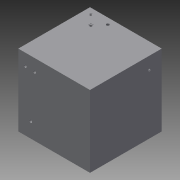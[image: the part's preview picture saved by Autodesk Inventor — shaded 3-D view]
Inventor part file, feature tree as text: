
AUTODESK INVENTOR PART (.ipt)
format: ipt  version: 2014 (Build 180170000, 170)  size: 350,208 bytes
history: native  units: mm
features: other x54, sketch x15, extrude x1
ambient origin geometry x8: Origin, YZ Plane, XZ Plane, XY Plane, X Axis, Y Axis, Z Axis, Center Point
bodies: 实体1 (feature_tree)
feature tree (70):
  extrude  "拉伸1"  TaperAngle=0.0deg  [1 undecoded]
  other  "UCS1"
  other  "UCS2"
  other  "UCS3"
  other  "UCS4"
  other  "UCS5"
  other  "UCS6"
  other  "iFeature7:2"
  other  "iFeature7:3"
  other  "iFeature7:4"
  other  "iFeature7:5"
  other  "iFeature7:6"
  other  "iFeature7:7"
  sketch  "草图1"  dims[d0=400.0mm d1=0.0mm]
  other  "UCS1: YZ 平面"
  other  "UCS1: XZ 平面"
  other  "UCS1: XY 平面"
  other  "UCS1: X 轴"
  other  "UCS1: Y 轴"
  other  "UCS1: Z 轴"
  other  "UCS1: 原点"
  other  "UCS2: YZ 平面"
  other  "UCS2: XZ 平面"
  other  "UCS2: XY 平面"
  other  "UCS2: X 轴"
  other  "UCS2: Y 轴"
  other  "UCS2: Z 轴"
  other  "UCS2: 原点"
  other  "UCS3: YZ 平面"
  other  "UCS3: XZ 平面"
  other  "UCS3: XY 平面"
  other  "UCS3: X 轴"
  other  "UCS3: Y 轴"
  other  "UCS3: Z 轴"
  other  "UCS3: 原点"
  other  "UCS4: YZ 平面"
  other  "UCS4: XZ 平面"
  other  "UCS4: XY 平面"
  other  "UCS4: X 轴"
  other  "UCS4: Y 轴"
  other  "UCS4: Z 轴"
  other  "UCS4: 原点"
  other  "UCS5: YZ 平面"
  other  "UCS5: XZ 平面"
  other  "UCS5: XY 平面"
  other  "UCS5: X 轴"
  other  "UCS5: Y 轴"
  other  "UCS5: Z 轴"
  other  "UCS5: 原点"
  other  "UCS6: YZ 平面"
  other  "UCS6: XZ 平面"
  other  "UCS6: XY 平面"
  other  "UCS6: X 轴"
  other  "UCS6: Y 轴"
  other  "UCS6: Z 轴"
  other  "UCS6: 原点"
  sketch  "草图2"  dims[d2=0.0mm d3=0.0mm d4=0.0mm d5=0.0mm d6=0.0mm d7=0.0mm]
  sketch  "草图3"  dims[d8=0.0mm d9=0.0mm d10=0.0mm d11=0.0mm d12=0.0mm d13=0.0mm]
  sketch  "草图4"  dims[d14=0.0mm d15=0.0mm d16=0.0mm d17=0.0mm d18=0.0mm d19=0.0mm]
  sketch  "草图5"  dims[d20=0.0mm d21=0.0mm d22=0.0mm d23=0.0mm d24=0.0mm d25=0.0mm]
  sketch  "草图6"  dims[d26=0.0mm d27=0.0mm d28=0.0mm d29=0.0mm d30=0.0mm d31=0.0mm]
  sketch  "草图8"  dims[d32=0.0mm d33=0.0mm d34=0.0mm d35=0.0mm d36=0.0mm d37=0.0mm d38=0.0mm]
  sketch  "草图10"  dims[d42=0.0mm]
  sketch  "草图11"  dims[d46=0.0mm]
  sketch  "草图12"  dims[d50=0.0mm]
  sketch  "草图13"  dims[d54=0.0mm]
  sketch  "草图14"  dims[d58=0.0mm]
  sketch  "草图15"  dims[d62=0.0mm]
  sketch  "草图16"  dims[d66=0.0mm]
  sketch  "草图17"  dims[d76=0.0mm d92=0.0mm]
note: 1 required parameter value undecoded (feature->parameter linkage not recoverable at this tier; creation-order binding heuristic only, values carry confidence <= 0.55)
